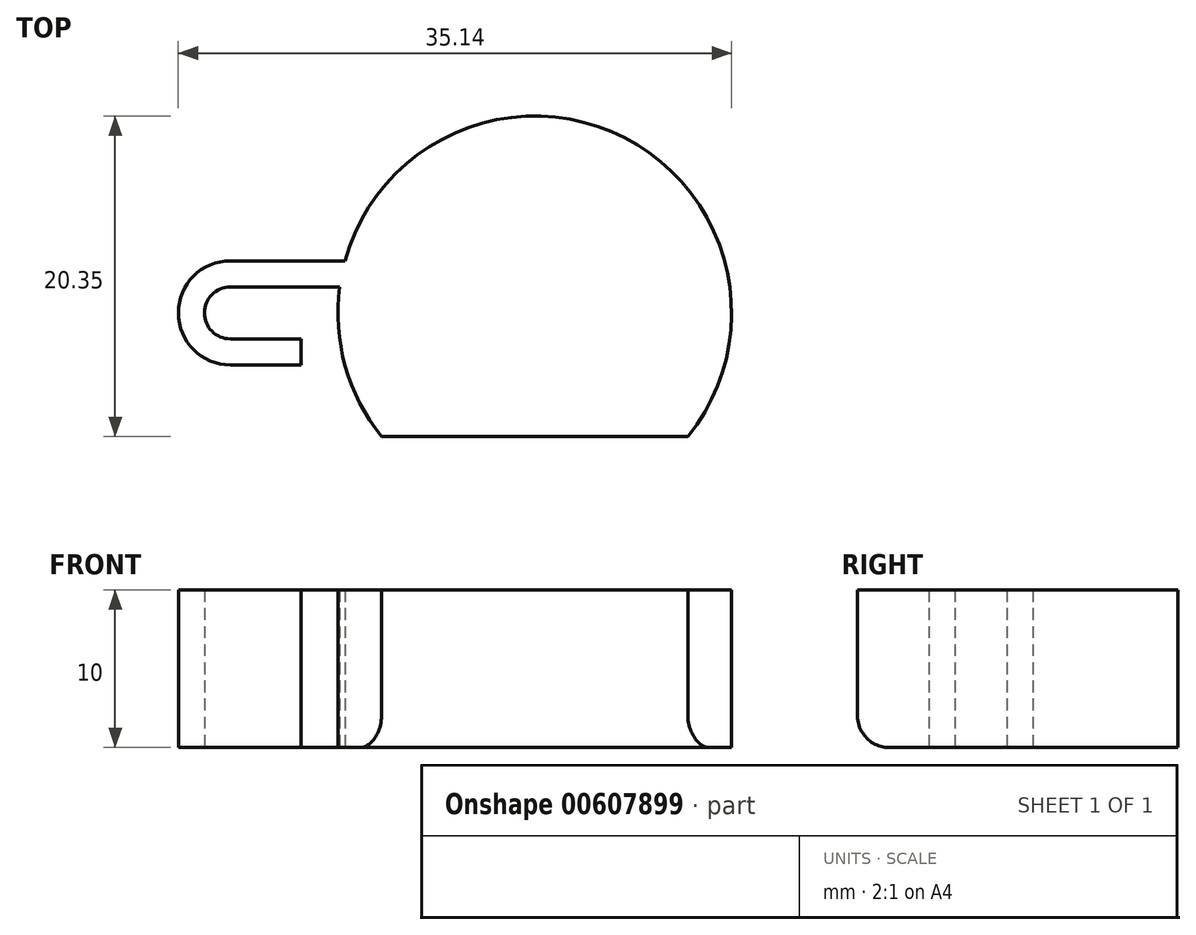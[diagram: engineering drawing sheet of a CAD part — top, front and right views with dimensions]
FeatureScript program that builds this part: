
annotation { "Feature Type Name" : "Feature", "Feature Type Description" : "" }
export const myFeature = defineFeature(function(context is Context, id is Id, definition is map)
    precondition{}
    {
        {
            var Q0;
            Q0=qCreatedBy(makeId("Top.planeOp"),FACE);
            var sketch = newSketch(context, id + "F0", { "sketchPlane" : qUnion([Q0])});
            skCircle(sketch, "E0", {"center": v(0, 0) * mm, "radius": 10.35 * mm});
            skLineSegment(sketch, "E1.bottom", {"start": v(10.35, 7.85) * mm, "end": v(-10.35, 7.85) * mm});
            skLineSegment(sketch, "E1.top", {"start": v(10.35, -7.85) * mm, "end": v(-10.35, -7.85) * mm});
            skLineSegment(sketch, "E1.left", {"start": v(10.35, 7.85) * mm, "end": v(10.35, -7.85) * mm});
            skLineSegment(sketch, "E1.right", {"start": v(-10.35, 7.85) * mm, "end": v(-10.35, -7.85) * mm});
            skCircle(sketch, "E2", {"center": v(0, 0) * mm, "radius": 12.5 * mm});
            skCircle(sketch, "E3", {"center": v(-19.33, 0) * mm, "radius": 1.65 * mm});
            skCircle(sketch, "E4", {"center": v(-19.33, 0) * mm, "radius": 3.3 * mm});
            skLineSegment(sketch, "E5.bottom", {"start": v(-15.84, 1.65) * mm, "end": v(-19.33, 1.65) * mm});
            skLineSegment(sketch, "E5.top", {"start": v(-15.84, -1.65) * mm, "end": v(-19.33, -1.65) * mm});
            skLineSegment(sketch, "E5.left", {"start": v(-15.84, 1.65) * mm, "end": v(-15.84, -1.65) * mm});
            skLineSegment(sketch, "E5.right", {"start": v(-19.33, 1.65) * mm, "end": v(-19.33, -1.65) * mm});
            skPoint(sketch, "E5.middle", {"position": v(-17.59, 0) * mm});
            skLineSegment(sketch, "E6", {"start": v(-19.33, 0) * mm, "end": v(-19.33, 3.3) * mm, "construction": true});
            skLineSegment(sketch, "E7", {"start": v(-19.33, 3.3) * mm, "end": v(-12.06, 3.3) * mm});
            skLineSegment(sketch, "E8", {"start": v(-16.47, 1.65) * mm, "end": v(-12.4, 1.65) * mm});
            skLineSegment(sketch, "E9.bottom", {"start": v(-19.33, -1.65) * mm, "end": v(-14.83, -1.65) * mm});
            skLineSegment(sketch, "E9.top", {"start": v(-19.33, -3.3) * mm, "end": v(-14.83, -3.3) * mm});
            skLineSegment(sketch, "E9.left", {"start": v(-19.33, -1.65) * mm, "end": v(-19.33, -3.3) * mm});
            skLineSegment(sketch, "E9.right", {"start": v(-14.83, -1.65) * mm, "end": v(-14.83, -3.3) * mm});
            skSolve(sketch);
        }
        {
            var Q0;
            {var subQ4=sQuery(id+"F0.wireOp",EDGE,"E5.bottom");Q0=makeQuery(id+"F0.imprint","IMPRINT",FACE,{"disambiguationData":[TD([[makeQuery(id+"F0.imprint","IMPRINT",EDGE,{"derivedFrom":subQ4}),-1.0]])]});}
            var Q1;
            {var subQ0=sQuery(id+"F0.wireOp",EDGE,"E7");Q1=makeQuery(id+"F0.imprint","IMPRINT",FACE,{"disambiguationData":[TD([[makeQuery(id+"F0.imprint","IMPRINT",EDGE,{"derivedFrom":subQ0}),-1.0]])]});}
            var Q2;
            {var subQ0=sQuery(id+"F0.wireOp",EDGE,"E2");var subQ1=makeQuery(id+"F0.imprint","INTERSECT",VERTEX,{"derivedFrom":[subQ0,sQuery(id+"F0.wireOp",EDGE,"E7")]});Q2=makeQuery(id+"F0.imprint","IMPRINT",FACE,{"disambiguationData":[TD([[makeQuery(id+"F0.imprint","IMPRINT",EDGE,{"disambiguationData":[TD([[subQ1,-1.0]])],"derivedFrom":subQ0}),1.0]])]});}
            var Q3;
            {var subQ0=sQuery(id+"F0.wireOp",EDGE,"E1.bottom");var subQ1=sQuery(id+"F0.wireOp",EDGE,"E0");var subQ2=makeQuery(id+"F0.imprint","INTERSECT",VERTEX,{"disambiguationData":[OD(0.0)],"derivedFrom":[subQ1,subQ0]});Q3=makeQuery(id+"F0.imprint","IMPRINT",FACE,{"disambiguationData":[TD([[makeQuery(id+"F0.imprint","IMPRINT",EDGE,{"disambiguationData":[TD([[subQ2,-1.0]])],"derivedFrom":subQ1}),-1.0]])]});}
            var Q4;
            {var subQ0=sQuery(id+"F0.wireOp",EDGE,"E1.bottom");var subQ1=sQuery(id+"F0.wireOp",EDGE,"E0");var subQ2=makeQuery(id+"F0.imprint","INTERSECT",VERTEX,{"disambiguationData":[OD(0.0)],"derivedFrom":[subQ1,subQ0]});Q4=makeQuery(id+"F0.imprint","IMPRINT",FACE,{"disambiguationData":[TD([[makeQuery(id+"F0.imprint","IMPRINT",EDGE,{"disambiguationData":[TD([[subQ2,-1.0]])],"derivedFrom":subQ1}),1.0]])]});}
            var Q5;
            {var subQ0=sQuery(id+"F0.wireOp",EDGE,"E1.top");var subQ1=sQuery(id+"F0.wireOp",EDGE,"E0");var subQ2=makeQuery(id+"F0.imprint","INTERSECT",VERTEX,{"disambiguationData":[OD(0.0)],"derivedFrom":[subQ1,subQ0]});Q5=makeQuery(id+"F0.imprint","IMPRINT",FACE,{"disambiguationData":[TD([[makeQuery(id+"F0.imprint","IMPRINT",EDGE,{"disambiguationData":[TD([[subQ2,-1.0]])],"derivedFrom":subQ1}),-1.0]])]});}
            var Q6;
            {var subQ0=sQuery(id+"F0.wireOp",EDGE,"E1.top");var subQ1=sQuery(id+"F0.wireOp",EDGE,"E0");var subQ2=makeQuery(id+"F0.imprint","INTERSECT",VERTEX,{"disambiguationData":[OD(0.0)],"derivedFrom":[subQ1,subQ0]});Q6=makeQuery(id+"F0.imprint","IMPRINT",FACE,{"disambiguationData":[TD([[makeQuery(id+"F0.imprint","IMPRINT",EDGE,{"disambiguationData":[TD([[subQ2,-1.0]])],"derivedFrom":subQ1}),1.0]])]});}
            var Q7;
            {var subQ1=sQuery(id+"F0.wireOp",EDGE,"E1.left");var subQ3=makeQuery(id+"F0.imprint","INTERSECT",VERTEX,{"derivedFrom":[sQuery(id+"F0.wireOp",EDGE,"E0"),subQ1]});Q7=makeQuery(id+"F0.imprint","IMPRINT",FACE,{"disambiguationData":[TD([[makeQuery(id+"F0.imprint","IMPRINT",EDGE,{"disambiguationData":[TD([[subQ3,1.0]])],"derivedFrom":subQ1}),1.0]])]});}
            var Q8;
            {var subQ0=sQuery(id+"F0.wireOp",EDGE,"E1.bottom");var subQ1=sQuery(id+"F0.wireOp",EDGE,"E0");var subQ2=makeQuery(id+"F0.imprint","INTERSECT",VERTEX,{"disambiguationData":[OD(1.0)],"derivedFrom":[subQ1,subQ0]});Q8=makeQuery(id+"F0.imprint","IMPRINT",FACE,{"disambiguationData":[TD([[makeQuery(id+"F0.imprint","IMPRINT",EDGE,{"disambiguationData":[TD([[subQ2,-1.0]])],"derivedFrom":subQ1}),-1.0]])]});}
            var Q9;
            {var subQ0=sQuery(id+"F0.wireOp",EDGE,"E1.right");var subQ1=sQuery(id+"F0.wireOp",EDGE,"E0");var subQ2=makeQuery(id+"F0.imprint","INTERSECT",VERTEX,{"derivedFrom":[subQ1,subQ0]});Q9=makeQuery(id+"F0.imprint","IMPRINT",FACE,{"disambiguationData":[TD([[makeQuery(id+"F0.imprint","IMPRINT",EDGE,{"disambiguationData":[TD([[subQ2,-1.0]])],"derivedFrom":subQ1}),-1.0]])]});}
            var Q10;
            {var subQ0=sQuery(id+"F0.wireOp",EDGE,"E1.left");var subQ1=sQuery(id+"F0.wireOp",EDGE,"E0");var subQ2=makeQuery(id+"F0.imprint","INTERSECT",VERTEX,{"derivedFrom":[subQ1,subQ0]});Q10=makeQuery(id+"F0.imprint","IMPRINT",FACE,{"disambiguationData":[TD([[makeQuery(id+"F0.imprint","IMPRINT",EDGE,{"disambiguationData":[TD([[subQ2,1.0]])],"derivedFrom":subQ1}),-1.0]])]});}
            var Q11;
            {var subQ0=sQuery(id+"F0.wireOp",EDGE,"E1.bottom");var subQ1=sQuery(id+"F0.wireOp",EDGE,"E0");var subQ2=makeQuery(id+"F0.imprint","INTERSECT",VERTEX,{"disambiguationData":[OD(0.0)],"derivedFrom":[subQ1,subQ0]});Q11=makeQuery(id+"F0.imprint","IMPRINT",FACE,{"disambiguationData":[TD([[makeQuery(id+"F0.imprint","IMPRINT",EDGE,{"disambiguationData":[TD([[subQ2,1.0]])],"derivedFrom":subQ1}),-1.0]])]});}
            var Q12;
            {var subQ0=sQuery(id+"F0.wireOp",EDGE,"E9.top");Q12=makeQuery(id+"F0.imprint","IMPRINT",FACE,{"disambiguationData":[TD([[makeQuery(id+"F0.imprint","IMPRINT",EDGE,{"derivedFrom":subQ0}),1.0]])]});}
            var Q13;
            {var subQ0=sQuery(id+"F0.wireOp",EDGE,"E9.left");Q13=makeQuery(id+"F0.imprint","IMPRINT",FACE,{"disambiguationData":[TD([[makeQuery(id+"F0.imprint","IMPRINT",EDGE,{"derivedFrom":subQ0}),1.0]])]});}
            extrude(context, id + "F1", {"entities" : qUnion([Q0, Q1, Q2, Q3, Q4, Q5, Q6, Q7, Q8, Q9, Q10, Q11, Q12, Q13]), "depth" : 10 * mm, "offsetDistance" : 25 * mm});
        }
        {
            var Q0;
            Q0=makeQuery(id+"F1.opExtrude","CAP_EDGE",EDGE,{"disambiguationData":[OSD([sQuery(id+"F0.wireOp",EDGE,"E1.bottom")])],"isStart":true});
            var Q1;
            Q1=makeQuery(id+"F1.opExtrude","CAP_EDGE",EDGE,{"disambiguationData":[OSD([sQuery(id+"F0.wireOp",EDGE,"E1.top")])],"isStart":true});
            var Q2;
            {var subQ0=sQuery(id+"F0.wireOp",EDGE,"E0");var subQ1=makeQuery(id+"F0.imprint","INTERSECT",VERTEX,{"derivedFrom":[subQ0,sQuery(id+"F0.wireOp",EDGE,"E1.right")]});Q2=makeQuery(id+"F1.opExtrude","CAP_EDGE",EDGE,{"disambiguationData":[OSD([subQ0]),TDD([makeQuery(id+"F0.imprint","IMPRINT",EDGE,{"disambiguationData":[TD([[makeQuery(id+"F0.imprint","INTERSECT",VERTEX,{"disambiguationData":[OD(1.0)],"derivedFrom":[subQ0,sQuery(id+"F0.wireOp",EDGE,"E1.bottom")]}),-1.0]])],"derivedFrom":subQ0}),makeQuery(id+"F0.imprint","IMPRINT",EDGE,{"disambiguationData":[TD([[subQ1,-1.0]])],"derivedFrom":subQ0})])],"isStart":true});}
            var Q3;
            {var subQ0=sQuery(id+"F0.wireOp",EDGE,"E0");var subQ1=makeQuery(id+"F0.imprint","INTERSECT",VERTEX,{"derivedFrom":[subQ0,sQuery(id+"F0.wireOp",EDGE,"E1.left")]});Q3=makeQuery(id+"F1.opExtrude","CAP_EDGE",EDGE,{"disambiguationData":[OSD([subQ0]),TDD([makeQuery(id+"F0.imprint","IMPRINT",EDGE,{"disambiguationData":[TD([[makeQuery(id+"F0.imprint","INTERSECT",VERTEX,{"disambiguationData":[OD(0.0)],"derivedFrom":[subQ0,sQuery(id+"F0.wireOp",EDGE,"E1.bottom")]}),1.0]])],"derivedFrom":subQ0}),makeQuery(id+"F0.imprint","IMPRINT",EDGE,{"disambiguationData":[TD([[subQ1,1.0]])],"derivedFrom":subQ0})])],"isStart":true});}
            fillet(context, id + "F2", {"entities" : qUnion([Q0, Q1, Q2, Q3]), "radius" : 2 * mm, "tangentPropagation" : true, "allowEdgeOverflow" : false});
        }
    });
